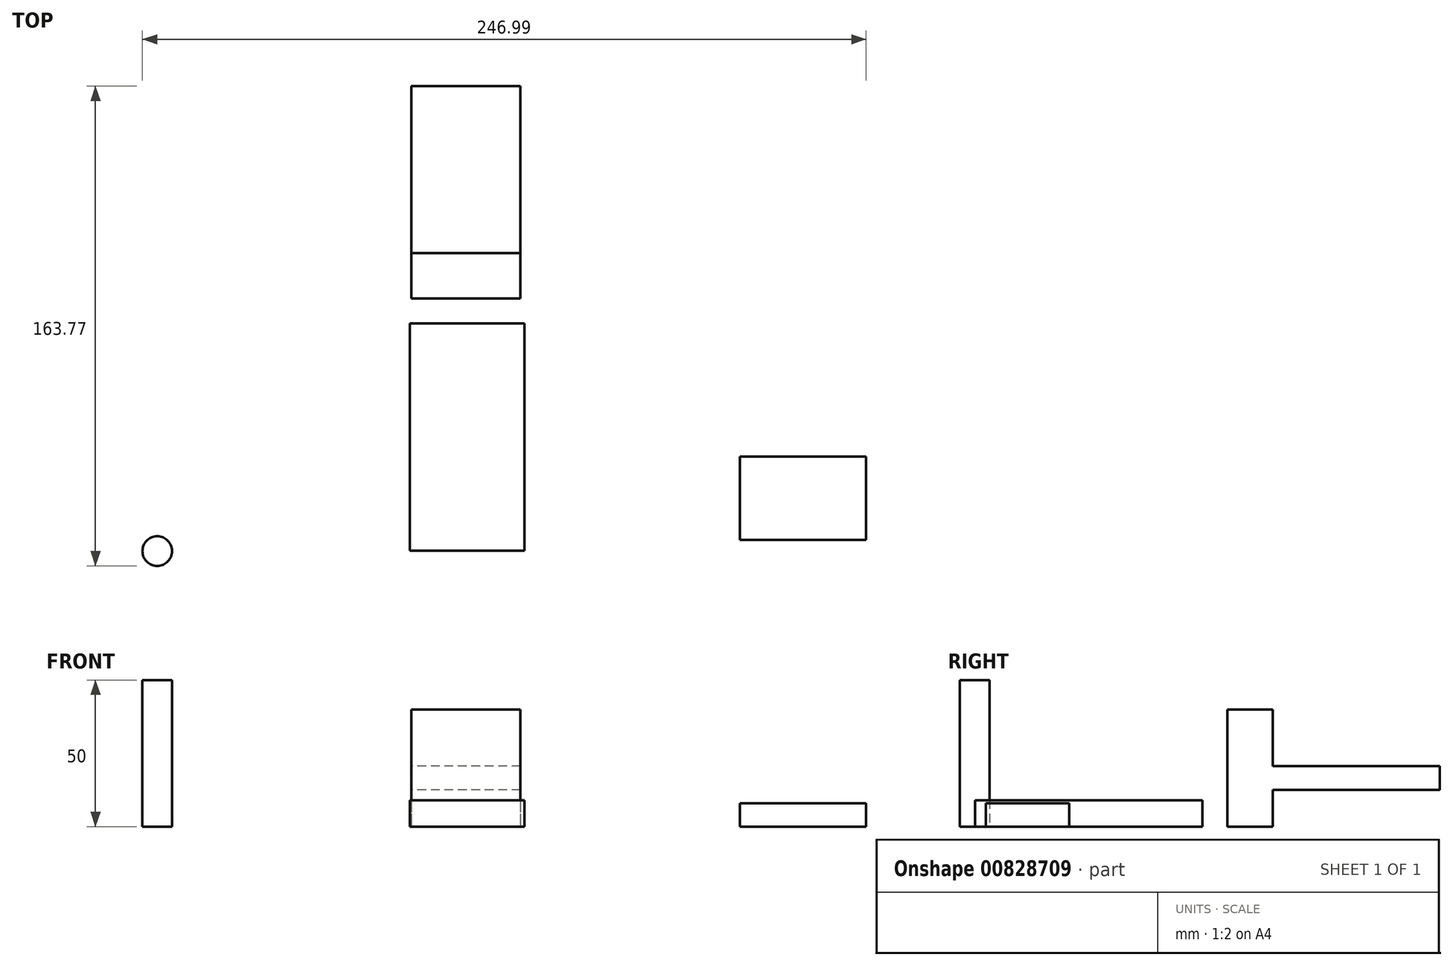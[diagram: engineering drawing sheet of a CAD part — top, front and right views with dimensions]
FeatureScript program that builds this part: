
annotation { "Feature Type Name" : "Feature", "Feature Type Description" : "" }
export const myFeature = defineFeature(function(context is Context, id is Id, definition is map)
    precondition{}
    {
        {
            var Q0;
            Q0=qCreatedBy(makeId("Top.planeOp"),FACE);
            var sketch = newSketch(context, id + "F0", { "sketchPlane" : qUnion([Q0])});
            skLineSegment(sketch, "E0.bottom", {"start": v(32.74, -56.52) * mm, "end": v(41.12, -56.52) * mm});
            skLineSegment(sketch, "E0.top", {"start": v(32.74, -51.7) * mm, "end": v(41.12, -51.7) * mm});
            skLineSegment(sketch, "E0.left", {"start": v(32.74, -56.52) * mm, "end": v(32.74, -51.7) * mm});
            skLineSegment(sketch, "E0.right", {"start": v(41.12, -56.52) * mm, "end": v(41.12, -51.7) * mm});
            skLineSegment(sketch, "E1.bottom", {"start": v(3.27, -53.6) * mm, "end": v(11.65, -53.6) * mm});
            skLineSegment(sketch, "E1.top", {"start": v(3.27, -48.79) * mm, "end": v(11.65, -48.79) * mm});
            skLineSegment(sketch, "E1.left", {"start": v(3.27, -53.6) * mm, "end": v(3.27, -48.79) * mm});
            skLineSegment(sketch, "E1.right", {"start": v(11.65, -53.6) * mm, "end": v(11.65, -48.79) * mm});
            skSolve(sketch);
        }
        {
            var Q0;
            Q0=sQuery(id+"F0.wireOp",EDGE,"E1.left");
            var Q1;
            Q1=sQuery(id+"F0.wireOp",EDGE,"E1.right");
            var Q2;
            Q2=sQuery(id+"F0.wireOp",EDGE,"E1.bottom");
            var Q3;
            Q3=sQuery(id+"F0.wireOp",EDGE,"E1.top");
            var Q4;
            Q4=sQuery(id+"F0.wireOp",EDGE,"E0.bottom");
            var Q5;
            Q5=sQuery(id+"F0.wireOp",EDGE,"E0.left");
            var Q6;
            Q6=sQuery(id+"F0.wireOp",EDGE,"E0.top");
            var Q7;
            Q7=sQuery(id+"F0.wireOp",EDGE,"E0.right");
            extrude(context, id + "F1", {"bodyType" : ToolBodyType.SURFACE, "surfaceEntities" : qUnion([Q0, Q1, Q2, Q3, Q4, Q5, Q6, Q7]), "depth" : 7 * mm, "offsetDistance" : 25 * mm});
        }
        {
            var Q0;
            Q0=qCreatedBy(makeId("Top.planeOp"),FACE);
            var sketch = newSketch(context, id + "F2", { "sketchPlane" : qUnion([Q0])});
            skLineSegment(sketch, "E2.bottom", {"start": v(-11.46, -43.43) * mm, "end": v(27.72, -43.43) * mm});
            skLineSegment(sketch, "E2.top", {"start": v(-11.46, 34.16) * mm, "end": v(27.72, 34.16) * mm});
            skLineSegment(sketch, "E2.left", {"start": v(-11.46, -43.43) * mm, "end": v(-11.46, 34.16) * mm});
            skLineSegment(sketch, "E2.right", {"start": v(27.72, -43.43) * mm, "end": v(27.72, 34.16) * mm});
            skSolve(sketch);
        }
        {
            var Q0;
            Q0=makeQuery(id+"F2.imprint","IMPRINT",FACE,{"disambiguationData":[TD([[makeQuery(id+"F2.imprint","IMPRINT",EDGE,{"derivedFrom":sQuery(id+"F2.wireOp",EDGE,"E2.bottom")}),1.0]])]});
            extrude(context, id + "F3", {"entities" : qUnion([Q0]), "depth" : 9 * mm, "offsetDistance" : 25 * mm});
        }
        {
            var Q0;
            Q0=qCreatedBy(makeId("Top.planeOp"),FACE);
            var sketch = newSketch(context, id + "F4", { "sketchPlane" : qUnion([Q0])});
            skLineSegment(sketch, "E3.bottom", {"start": v(26.35, 42.7) * mm, "end": v(-10.9, 42.7) * mm});
            skLineSegment(sketch, "E3.top", {"start": v(26.35, 58.12) * mm, "end": v(-10.9, 58.12) * mm});
            skLineSegment(sketch, "E3.left", {"start": v(26.35, 42.7) * mm, "end": v(26.35, 58.12) * mm});
            skLineSegment(sketch, "E3.right", {"start": v(-10.9, 42.7) * mm, "end": v(-10.9, 58.12) * mm});
            skSolve(sketch);
        }
        {
            var Q0;
            Q0=makeQuery(id+"F4.imprint","IMPRINT",FACE,{"disambiguationData":[TD([[makeQuery(id+"F4.imprint","IMPRINT",EDGE,{"derivedFrom":sQuery(id+"F4.wireOp",EDGE,"E3.bottom")}),-1.0]])]});
            extrude(context, id + "F5", {"entities" : qUnion([Q0]), "depth" : 40 * mm, "offsetDistance" : 25 * mm});
        }
        {
            var Q0;
            Q0=makeQuery(id+"F5.opExtrude","SWEPT_FACE",FACE,{"disambiguationData":[OSD([sQuery(id+"F4.wireOp",EDGE,"E3.top")])]});
            var sketch = newSketch(context, id + "F6", { "sketchPlane" : qUnion([Q0])});
            skLineSegment(sketch, "E4.bottom", {"start": v(-26.35, 20.63) * mm, "end": v(10.9, 20.63) * mm});
            skLineSegment(sketch, "E4.top", {"start": v(-26.35, 12.51) * mm, "end": v(10.9, 12.51) * mm});
            skLineSegment(sketch, "E4.left", {"start": v(-26.35, 20.63) * mm, "end": v(-26.35, 12.51) * mm});
            skLineSegment(sketch, "E4.right", {"start": v(10.9, 20.63) * mm, "end": v(10.9, 12.51) * mm});
            skSolve(sketch);
        }
        {
            var Q0;
            Q0=makeQuery(id+"F6.imprint","IMPRINT",FACE,{"disambiguationData":[TD([[makeQuery(id+"F6.imprint","IMPRINT",EDGE,{"derivedFrom":sQuery(id+"F6.wireOp",EDGE,"E4.bottom")}),-1.0]])]});
            extrude(context, id + "F7", {"entities" : qUnion([Q0]), "operationType" : NewBodyOperationType.ADD, "depth" : 16 * mm, "offsetDistance" : 25 * mm});
        }
        {
            var Q0;
            Q0=makeQuery(id+"F7.opExtrude","CAP_FACE",FACE,{"disambiguationData":[OSD([sQuery(id+"F6.wireOp",EDGE,"E4.bottom"),sQuery(id+"F6.wireOp",EDGE,"E4.top"),sQuery(id+"F6.wireOp",EDGE,"E4.left"),sQuery(id+"F6.wireOp",EDGE,"E4.right")])],"isStart":false});
            extrude(context, id + "F8", {"entities" : qUnion([Q0]), "operationType" : NewBodyOperationType.ADD, "depth" : 25 * mm, "offsetDistance" : 25 * mm});
        }
        {
            var Q0;
            Q0=makeQuery(id+"F8.opExtrude","CAP_FACE",FACE,{"disambiguationData":[OSD([sQuery(id+"F6.wireOp",EDGE,"E4.bottom"),sQuery(id+"F6.wireOp",EDGE,"E4.top"),sQuery(id+"F6.wireOp",EDGE,"E4.left"),sQuery(id+"F6.wireOp",EDGE,"E4.right")])],"isStart":false});
            extrude(context, id + "F9", {"entities" : qUnion([Q0]), "operationType" : NewBodyOperationType.ADD, "depth" : 15 * mm, "offsetDistance" : 25 * mm});
        }
        {
            var Q0;
            Q0=makeQuery(id+"F9.opExtrude","CAP_FACE",FACE,{"disambiguationData":[OSD([sQuery(id+"F6.wireOp",EDGE,"E4.bottom"),sQuery(id+"F6.wireOp",EDGE,"E4.top"),sQuery(id+"F6.wireOp",EDGE,"E4.left"),sQuery(id+"F6.wireOp",EDGE,"E4.right")])],"isStart":false});
            extrude(context, id + "F10", {"entities" : qUnion([Q0]), "operationType" : NewBodyOperationType.ADD, "depth" : 1 * mm, "offsetDistance" : 25 * mm});
        }
        {
            var Q0;
            Q0=makeQuery(id+"F10.opExtrude","CAP_FACE",FACE,{"disambiguationData":[OSD([sQuery(id+"F6.wireOp",EDGE,"E4.bottom"),sQuery(id+"F6.wireOp",EDGE,"E4.top"),sQuery(id+"F6.wireOp",EDGE,"E4.left"),sQuery(id+"F6.wireOp",EDGE,"E4.right")])],"isStart":false});
            extrude(context, id + "F11", {"entities" : qUnion([Q0]), "operationType" : NewBodyOperationType.ADD, "depth" : -20 * mm, "offsetDistance" : 25 * mm});
        }
        {
            var Q0;
            Q0=qCreatedBy(makeId("Top.planeOp"),FACE);
            var sketch = newSketch(context, id + "F12", { "sketchPlane" : qUnion([Q0])});
            skCircle(sketch, "E5", {"center": v(-97.66, -43.6) * mm, "radius": 5.05 * mm});
            skSolve(sketch);
        }
        {
            var Q0;
            Q0=makeQuery(id+"F12.imprint","IMPRINT",FACE,{"disambiguationData":[TD([[makeQuery(id+"F12.imprint","IMPRINT",EDGE,{"derivedFrom":sQuery(id+"F12.wireOp",EDGE,"E5")}),1.0]])]});
            extrude(context, id + "F13", {"entities" : qUnion([Q0]), "depth" : 50 * mm, "offsetDistance" : 25 * mm});
        }
        {
            var Q0;
            Q0=qCreatedBy(makeId("Top.planeOp"),FACE);
            var sketch = newSketch(context, id + "F14", { "sketchPlane" : qUnion([Q0])});
            skLineSegment(sketch, "E6.bottom", {"start": v(101.16, -11.28) * mm, "end": v(144.28, -11.28) * mm});
            skLineSegment(sketch, "E6.top", {"start": v(101.16, -39.74) * mm, "end": v(144.28, -39.74) * mm});
            skLineSegment(sketch, "E6.left", {"start": v(101.16, -11.28) * mm, "end": v(101.16, -39.74) * mm});
            skLineSegment(sketch, "E6.right", {"start": v(144.28, -11.28) * mm, "end": v(144.28, -39.74) * mm});
            skSolve(sketch);
        }
        {
            var Q0;
            Q0=makeQuery(id+"F14.imprint","IMPRINT",FACE,{"disambiguationData":[TD([[makeQuery(id+"F14.imprint","IMPRINT",EDGE,{"derivedFrom":sQuery(id+"F14.wireOp",EDGE,"E6.bottom")}),-1.0]])]});
            extrude(context, id + "F15", {"entities" : qUnion([Q0]), "depth" : 8 * mm, "offsetDistance" : 25 * mm});
        }
    });
